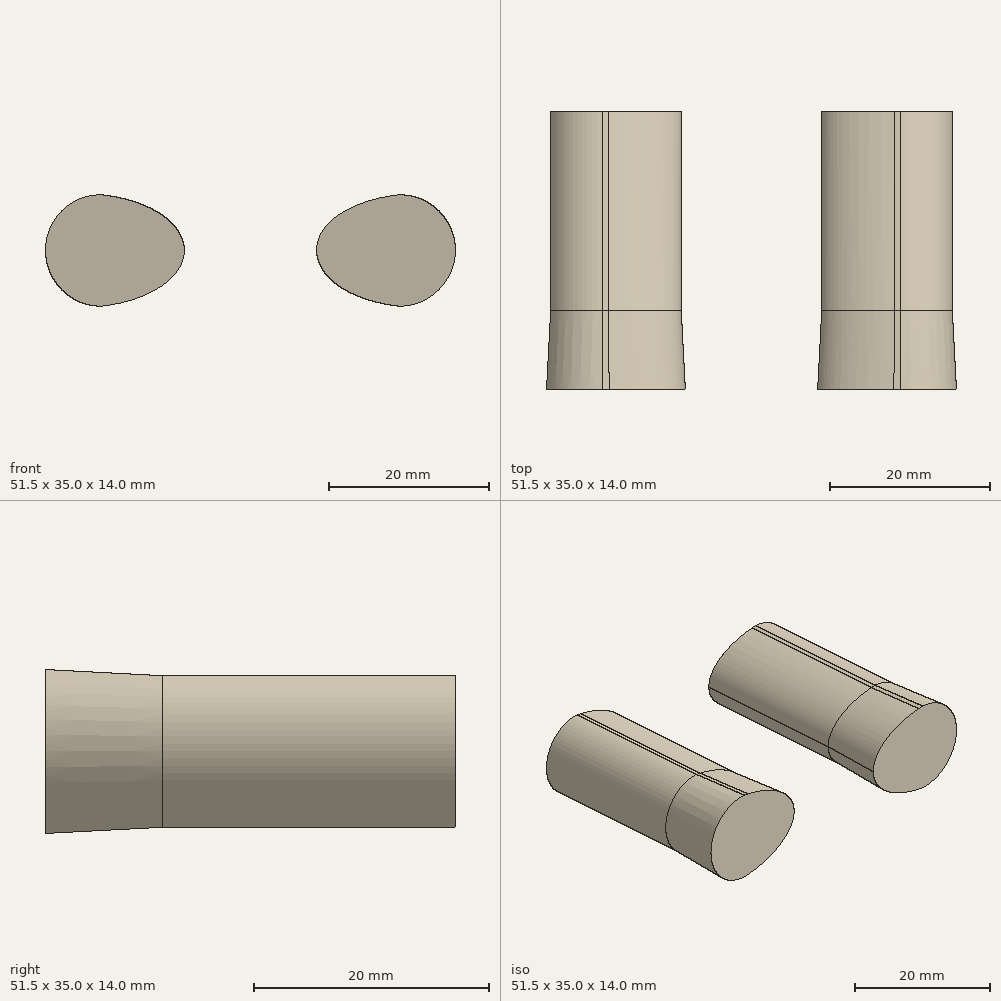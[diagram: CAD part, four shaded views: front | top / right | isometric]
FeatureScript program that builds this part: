
annotation { "Feature Type Name" : "Feature", "Feature Type Description" : "" }
export const myFeature = defineFeature(function(context is Context, id is Id, definition is map)
    precondition{}
    {
        {
            var Q0;
            Q0=qCreatedBy(makeId("Front.planeOp"),FACE);
            var sketch = newSketch(context, id + "F0", { "sketchPlane" : qUnion([Q0])});
            skArc(sketch, "E0.126.MirrorCS", {"start": v(11.09, 7.64) * mm, "mid": v(8.06, 2.38) * mm, "end": v(2.31, 0.43) * mm});
            skArc(sketch, "E0.93.MirrorCS", {"start": v(2.5, 2.5) * mm, "mid": v(9.01, 8.97) * mm, "end": v(2.5, 15.45) * mm});
            skLineSegment(sketch, "E0.149.MirrorCS", {"start": v(11.22, 8.98) * mm, "end": v(-15.96, 8.98) * mm, "construction": true});
            skEllipticalArc(sketch, "E0.111.MirrorCS", {});
            skEllipticalArc(sketch, "E1.0.MirrorCS", {});
            skEllipticalArc(sketch, "E2.0.MirrorCS", {});
            skPoint(sketch, "E0.66.MirrorP", {"position": v(-7.37, 8.98) * mm});
            skLineSegment(sketch, "E0.163.MirrorCS", {"start": v(-4.82, 16.13) * mm, "end": v(-12.2, 10.48) * mm});
            skPoint(sketch, "E0.88.MirrorP", {"position": v(-25.01, 8.98) * mm});
            skLineSegment(sketch, "E0.127.MirrorCS", {"start": v(-27.57, 1.82) * mm, "end": v(-20.2, 7.48) * mm});
            skLineSegment(sketch, "E0.174.MirrorCS", {"start": v(-27.57, 16.13) * mm, "end": v(-20.2, 10.48) * mm});
            skEllipticalArc(sketch, "E0.90.MirrorCS", {});
            skEllipticalArc(sketch, "E3.19.MirrorCS", {});
            skEllipticalArc(sketch, "E0.125.MirrorCS", {});
            skEllipticalArc(sketch, "E3.2.MirrorCS", {});
            skArc(sketch, "E0.142.MirrorCS", {"start": v(11.09, 7.64) * mm, "mid": v(8.06, 2.38) * mm, "end": v(2.31, 0.43) * mm});
            skArc(sketch, "E0.80.MirrorCS", {"start": v(11.09, 10.31) * mm, "mid": v(8.06, 15.57) * mm, "end": v(2.31, 17.52) * mm});
            skArc(sketch, "E0.123.MirrorCS", {"start": v(2.5, 15.45) * mm, "mid": v(9.01, 8.98) * mm, "end": v(2.5, 2.5) * mm});
            skEllipticalArc(sketch, "E0.73.MirrorCS", {});
            skEllipticalArc(sketch, "E0.145.MirrorCS", {});
            skEllipticalArc(sketch, "E0.175.MirrorCS", {});
            skEllipticalArc(sketch, "E0.81.MirrorCS", {});
            skPoint(sketch, "E0.165.MirrorP", {"position": v(-7.37, 8.98) * mm});
            skLineSegment(sketch, "E0.166.MirrorCS", {"start": v(-4.82, 1.82) * mm, "end": v(-12.2, 7.48) * mm});
            skEllipticalArc(sketch, "E3.16.MirrorCS", {});
            skEllipticalArc(sketch, "E3.15.MirrorCS", {});
            skEllipticalArc(sketch, "E3.13.MirrorCS", {});
            skArc(sketch, "E0.76.MirrorCS", {"start": v(11.09, 10.31) * mm, "mid": v(8.06, 15.57) * mm, "end": v(2.31, 17.52) * mm});
            skEllipticalArc(sketch, "E0.108.MirrorCS", {});
            skEllipticalArc(sketch, "E0.154.MirrorCS", {});
            skEllipticalArc(sketch, "E0.153.MirrorCS", {});
            skPoint(sketch, "E0.139.MirrorP", {"position": v(7.37, 8.98) * mm});
            skEllipticalArc(sketch, "E3.11.MirrorCS", {});
            skEllipticalArc(sketch, "E0.124.MirrorCS", {});
            skEllipticalArc(sketch, "E3.6.MirrorCS", {});
            skEllipticalArc(sketch, "E0.63.MirrorCS", {});
            skEllipticalArc(sketch, "E0.112.MirrorCS", {});
            skEllipticalArc(sketch, "E0.50.MirrorCS", {});
            skEllipticalArc(sketch, "E0.56.MirrorCS", {});
            skLineSegment(sketch, "E0.35.MirrorCS", {"start": v(-12.2, 10.48) * mm, "end": v(-16.2, 10.48) * mm});
            skLineSegment(sketch, "E0.48.MirrorCS", {"start": v(-20.2, 10.48) * mm, "end": v(-16.2, 10.48) * mm});
            skLineSegment(sketch, "E0.150.MirrorCS", {"start": v(-12.2, 7.48) * mm, "end": v(-16.2, 7.48) * mm});
            skLineSegment(sketch, "E0.15.MirrorCS", {"start": v(-16.2, 10.48) * mm, "end": v(-16.2, 7.48) * mm, "construction": true});
            skArc(sketch, "E0.51.MirrorCS", {"start": v(11.22, 8.98) * mm, "mid": v(11.18, 8.3) * mm, "end": v(11.09, 7.64) * mm});
            skArc(sketch, "E0.5.MirrorCS", {"start": v(11.22, 8.98) * mm, "mid": v(11.18, 9.65) * mm, "end": v(11.09, 10.31) * mm});
            skLineSegment(sketch, "E0.53.MirrorCS", {"start": v(-4.82, 1.82) * mm, "end": v(-4.9, 1.88) * mm});
            skLineSegment(sketch, "E0.41.MirrorCS", {"start": v(-4.82, 16.13) * mm, "end": v(-4.9, 16.07) * mm});
            skArc(sketch, "E0.83.MirrorCS", {"start": v(11.22, 8.98) * mm, "mid": v(11.18, 8.3) * mm, "end": v(11.09, 7.64) * mm});
            skArc(sketch, "E0.9.MirrorCS", {"start": v(11.22, 8.98) * mm, "mid": v(11.18, 9.65) * mm, "end": v(11.09, 10.31) * mm});
            skArc(sketch, "E0.140.MirrorCS", {"start": v(-43.48, 10.31) * mm, "mid": v(-40.45, 15.57) * mm, "end": v(-34.7, 17.52) * mm});
            skLineSegment(sketch, "E0.24.MirrorCS", {"start": v(-4.84, 1.84) * mm, "end": v(-4.9, 1.88) * mm});
            skArc(sketch, "E0.130.MirrorCS", {"start": v(-43.48, 10.31) * mm, "mid": v(-40.45, 15.57) * mm, "end": v(-34.7, 17.52) * mm});
            skArc(sketch, "E0.17.MirrorCS", {"start": v(-43.6, 8.98) * mm, "mid": v(-43.57, 8.3) * mm, "end": v(-43.48, 7.64) * mm});
            skArc(sketch, "E0.2.MirrorCS", {"start": v(-43.6, 8.98) * mm, "mid": v(-43.57, 9.65) * mm, "end": v(-43.48, 10.31) * mm});
            skArc(sketch, "E0.49.MirrorCS", {"start": v(-43.6, 8.98) * mm, "mid": v(-43.57, 8.3) * mm, "end": v(-43.48, 7.64) * mm});
            skArc(sketch, "E0.12.MirrorCS", {"start": v(-43.6, 8.98) * mm, "mid": v(-43.57, 9.65) * mm, "end": v(-43.48, 10.31) * mm});
            skArc(sketch, "E0.129.MirrorCS", {"start": v(-43.48, 7.64) * mm, "mid": v(-40.45, 2.38) * mm, "end": v(-34.7, 0.43) * mm});
            const initialGuessF0  = {"E0.111.MirrorCS": [0.0030514923956593137, 0.009124177164707922, -0.9999662829908004, 0.008211752648659722, 0.014503835708598836, 0.008709066754360477, 0.9960291224734913, 1.524830246234359], "E0.145.MirrorCS": [0.005070347177176379, 0.008985480561974301, -0.999999973716248, 0.00022927604223292356, 0.012443666068111585, 0.006625561645583439, 0.0019968615783168848, 1.3628694689470184], "E1.0.MirrorCS": [0.005070265867908692, 0.008972474829462344, 0.9999999870544558, -0.0001609070794542438, 0.01244356297346729, 0.006616551052948457, 1.7786605351817808, 3.1414980146120013], "E2.0.MirrorCS": [0.0030514923956593207, 0.008826029376189187, 0.9999662829908004, 0.008211752648658827, 0.014503835708598836, 0.008709066754360471, 1.6167624073554339, 2.1455635311163026], "E0.90.MirrorCS": [-0.03745850227469059, 0.008985480561974336, 0.999999973716248, 0.00022927604223062453, 0.012443666068111585, 0.006625561645583439, 4.92031583823257, 6.281188445601268], "E3.19.MirrorCS": [-0.03745842096542284, 0.008972474829463364, 0.9999999870544558, 0.00016090707945387583, 0.01244356297346729, 0.006616551052948457, 9.463897763902778e-05, 1.3629321184073395], "E0.125.MirrorCS": [-0.035439647493173514, 0.009124177164707935, 0.9999662829908004, 0.00821175264865911, 0.014503835708598836, 0.008709066754360477, 4.7583550609452265, 5.287156184706094], "E3.2.MirrorCS": [-0.03543964749317352, 0.008826029376189318, 0.9999662829908004, -0.008211752648660859, 0.014503835708598836, 0.008709066754360477, 0.9960291224734886, 1.5248302462343595], "E0.73.MirrorCS": [0.0030514923956593207, 0.009124177164707908, -0.9999662829908004, 0.008211752648659806, 0.014503835708598836, 0.008709066754360471, 0.9960291224734906, 1.5248302462343584], "E0.145.MirrorCS": [0.005070347177176379, 0.008985480561974301, -0.999999973716248, 0.00022927604223292356, 0.012443666068111585, 0.006625561645583439, 0.0019968615783168848, 1.3628694689470184], "E0.175.MirrorCS": [0.005070265867908692, 0.008972474829462344, -0.9999999870544558, 0.0001609070794542438, 0.01244356297346729, 0.006616551052948457, 4.920253188771574, 6.283090668201794], "E0.81.MirrorCS": [0.0030514923956593137, 0.008826029376189173, -0.9999662829908004, -0.008211752648658744, 0.014503835708598836, 0.008709066754360477, 4.758355060945227, 5.287156184706094], "E3.16.MirrorCS": [-0.03745850227469057, 0.008985480561974325, 0.999999973716248, 0.00022927604223517984, 0.012443666068111585, 0.006625561645583439, 4.9203158382325665, 6.281188445601262], "E3.15.MirrorCS": [-0.037458502274690574, 0.008964725978923812, 0.999999973716248, -0.00022927604223497855, 0.012443666068111585, 0.006625561645583488, 0.0019968615781701853, 1.3628694689463623], "E3.13.MirrorCS": [-0.035439647493173514, 0.009124177164707935, -0.9999662829908004, -0.00821175264865911, 0.014503835708598836, 0.008709066754360477, 1.6167624073554334, 2.1455635311163013], "E0.133.MirrorCS": [-0.03543964749317352, 0.0088260293761892, 0.9999662829908004, -0.00821175264865944, 0.014503835708598836, 0.008709066754360471, 0.9960291224734907, 1.5248302462343577], "E0.111.MirrorCS": [0.0030514923956593137, 0.009124177164707922, -0.9999662829908004, 0.008211752648659722, 0.014503835708598836, 0.008709066754360477, 0.9960291224734913, 1.524830246234359], "E0.108.MirrorCS": [0.0050702658679086885, 0.008977731711435049, -0.9999999870544558, -0.00016090707947073046, 0.01244356297346729, 0.006616551052948622, 9.463897780343474e-05, 1.3629321184080052], "E0.154.MirrorCS": [0.005070347177176386, 0.008964725978922814, -0.999999973716248, -0.00022927604223816638, 0.012443666068111585, 0.006625561645583488, 4.920315838232565, 6.28118844560126], "E0.153.MirrorCS": [0.0030514923956593207, 0.008826029376189187, -0.9999662829908004, -0.008211752648658827, 0.014503835708598836, 0.008709066754360471, 4.758355060945227, 5.287156184706095], "E3.11.MirrorCS": [-0.037458420965422845, 0.008977731711434837, -0.9999999870544558, 0.0001609070794478293, 0.01244356297346729, 0.006616551052948457, 1.7786605351817724, 3.14149801461198], "E0.124.MirrorCS": [-0.03745850227469058, 0.008964725978922814, 0.999999973716248, -0.0002292760422403644, 0.012443666068111585, 0.006625561645583488, 0.001996861578330846, 1.3628694689470229], "E3.6.MirrorCS": [-0.03543964749317353, 0.009124177164707929, 0.9999662829908004, 0.008211752648658827, 0.014503835708598836, 0.008709066754360471, 4.758355060945227, 5.287156184706096], "E0.63.MirrorCS": [-0.035439647493173514, 0.008826029376189187, 0.9999662829908004, -0.008211752648659356, 0.014503835708598836, 0.008709066754360477, 0.9960291224734917, 1.524830246234359], "E0.112.MirrorCS": [-0.03745842096542283, 0.008977731711434837, 0.9999999870544558, -0.0001609070794520033, 0.01244356297346729, 0.006616551052948457, 4.920253188771566, 6.283090668201781], "E0.50.MirrorCS": [-0.03745842096542285, 0.008972474829460914, 0.9999999870544558, 0.0001609070794531974, 0.01244356297346729, 0.006616551052948457, 9.463897801049703e-05, 1.3629321184090444], "E0.56.MirrorCS": [-0.03543964749317352, 0.009124177164707922, 0.9999662829908004, 0.008211752648659193, 0.014503835708598836, 0.008709066754360471, 4.758355060945227, 5.287156184706095], "E3.17.MirrorCS": [-0.03543964749317352, 0.0088260293761892, 0.9999662829908004, -0.00821175264865944, 0.014503835708598836, 0.008709066754360471, 0.9960291224734906, 1.524830246234359]};
            skSetInitialGuess(sketch, initialGuessF0);
            skSolve(sketch);
        }
        {
            var Q0;
            Q0 = qSketchRegion(id + "F0", true);
            extrude(context, id + "F1", {"entities" : qUnion([Q0]), "depth" : 10 * mm, "hasDraft" : true, "draftAngle" : 3 * degree, "hasSecondDirection" : true, "secondDirectionOppositeDirection" : true, "secondDirectionDepth" : 25 * mm});
        }
    });
